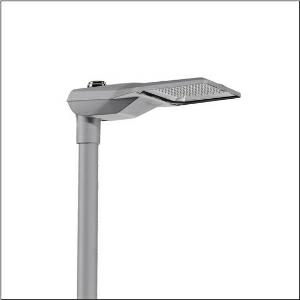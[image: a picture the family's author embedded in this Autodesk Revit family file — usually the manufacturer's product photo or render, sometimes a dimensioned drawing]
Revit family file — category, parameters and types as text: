
# Revit family: streetlight_sl_21_midi___stw1_0a_5xe7e37n08mb_6d50
name_source: partatom
category: Lighting Fixtures
units: mm (PartAtom-declared; Revit-internal decimal feet)

## family parameters
Cut with Voids When Loaded = No
Host = Face
Light Source = No
Part Type = Normal
Room Calculation Point = No
Round Connector Dimension = Use Diameter
Shared = No

## types (1)
- --- (1 x LED, 18270 lm, 136 W, 3000K)
    Apparent Load = 136 VA
    CIE Flux Codes = 38 75 98 100 100
    Color Rendering = 70
    Color Temperature = 3000K
    Default Elevation = 1800 mm
    Description = Streetlight SL 21 midi, mast luminaire, primary light control with lens, of PMMA, primary optical cover: cover, of toughened safety glass, transparent, light distribution: STW1.0a, light emission: direct distribution, primary light characteristic: asymmetric, installation type: side-entry, LED, 3G 2.5mm², High Power LED, rated luminous flux: 18.270lm, luminous efficacy: 134lm/W, light colour: 730, colour temperature: 3000K, control gear: NEMA (7pin), control: overheat protection, pre-setting: linear dimming characteristic, constant luminous flux control, time-dependent luminous flux control, flexible luminous flux parameterisation, mains connection: 220..240V, AC, 50/60Hz, connection cable pre-assembled, cable length: 12,5m, wiring characteristics: H05VV-F, start of lifetime: 136W, end of service life: 142W, reduction: 61W, luminaire housing, of diecast aluminium (EN AC-44300), powder-coated, Siteco® metallic grey (DB 702S), corrosivity category C5 mid according to DIN EN ISO 12944, multi-level sealing system, sealing non-destructively replaceable, inclination adjustable: 0°, 5°, 10°, 15°, length: 644mm, width: 335mm, height: 110mm, spigot size: 42mm (side-entry), mounting height: 4..8m, protection rating (complete): IP66, insulation class (complete): insulation class I (protective earthing), certification: CE, ENEC, ENEC+, VDE, impact resistance: IK10, permissible operating ambient temperature for outdoor applications: -40..+50°C, standard-compliant lighting for roads and squares, packaging unit: 1 piece

Light Distribution: STW1.0a
    Height = 111 mm
    Lamp = 1 x LED
    Lamp Light Flux = 18270 lm
    Lamp Power = 136 W
    Lamp count = 1
    Length = 644 mm
    Luminous efficacy = 134 lm/W
    Manufacturer = Siteco
    ModVariant = No
    Model = 5XE7E37N08MB
    Number of Poles = 1
    OnlyDefault = Yes
    Power Factor = 1
    Product Name = Streetlight SL 21 midi | STW1.0a
    Product group = mast luminaire | pylon top
    ProductGroupID = 6100
    Protection Class = Protection class I
    Protection Degree = IP 66
    RLX_Detail_Level = 1
    RLX_Emergency_Light_Flux = 0 lm
    RLX_Emergency_Type = 0
    RLX_Emergency_Type_DB = No
    RlxData = <blob elided: 26541 chars, md5=0b588021>
    Socket = socket
    Standby Power = 0 W
    System Light Flux = 18270 lm
    System Power = 136 W
    Type Comments = factory setting: luminous flux: 100 % | dim-lin: 254 | 695 mA
    Type Image = l_1294377.jpg
    URL = http://relux.com
    VarID = @adj_156999
    Voltage = 0 V
    Weight = 0.00 kg
    Width = 336 mm

## geometry (parser evidence)
native form markers: Blend x4, Sweep x12
no freeform markers — native parametric forms only
